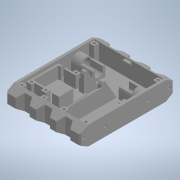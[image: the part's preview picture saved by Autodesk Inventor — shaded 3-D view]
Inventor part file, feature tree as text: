
AUTODESK INVENTOR PART (.ipt)
format: ipt  version: 2020 (Build 240168000, 168)  size: 1,044,992 bytes
history: native  units: in
note: dims shown in document units (in); Inventor stores cm internally (conversion verified against a paired STEP export)
features: projected_geometry x34, extrude x21, sketch x21, mirror x6, plane x1, chamfer x1
ambient origin geometry x8: Origin, YZ Plane, XZ Plane, XY Plane, X Axis, Y Axis, Z Axis, Center Point
bodies: Solid1 (feature_tree)
feature tree (84):
  extrude  "Extrusion1"  Depth=5.9055in
  extrude  "Extrusion2"  TaperAngle=0.0deg  [1 undecoded]
  extrude  "Extrusion3"  Depth=1.063in
  extrude  "Extrusion4"  Depth=0.315in
  extrude  "Extrusion5"  TaperAngle=0.0deg  [1 undecoded]
  extrude  "Extrusion6"  Depth=0.5906in
  mirror  "Mirror1"
  extrude  "Extrusion7"  Depth=0.0787in
  mirror  "Mirror2"
  extrude  "Extrusion8"  Depth=0.6102in
  mirror  "Mirror3"
  plane  "Work Plane1"
  extrude  "Extrusion9"  Depth=0.7874in TaperAngle=0.0deg
  mirror  "Mirror4"
  extrude  "Extrusion10"  Depth=6.063in TaperAngle=0.0deg
  extrude  "Extrusion11"  Depth=0.1575in
  sketch  "Sketch20"  dims[d27=1.5748in d28=0.0in d29=0.0in]
  extrude  "Extrusion17"  TaperAngle=0.0deg  [1 undecoded]
  extrude  "Extrusion19"  Depth=0.2756in
  mirror  "Mirror7"
  extrude  "Extrusion20"  Depth=0.4331in
  extrude  "Extrusion22"  Depth=2.7559in
  extrude  "Extrusion25"  Depth=0.0453in
  extrude  "Extrusion26"  TaperAngle=0.0deg  [1 undecoded]
  extrude  "Extrusion27"  Depth=0.0787in
  extrude  "Extrusion28"  Depth=0.993in
  extrude  "Extrusion29"  Depth=0.2756in
  sketch  "Sketch32"  dims[d46=0.315in d48=0.993in]
  extrude  "Extrusion30"  Depth=0.4724in
  mirror  "Mirror9"
  chamfer  "Chamfer1"  Distance=1.5748in
  sketch  "Sketch39"  dims[d54=0.0in d55=0.4724in d57=1.5748in d58=1.6142in d59=0.1181in d60=0.1969in d89=0.0157in d90=0.0157in d91=0.1476in d92=0.1476in d96=0.315in d97=0.1575in d98=0.1181in d99=0.0in d108=0.0394in d109=0.0in d110=0.063in d111=0.0394in d112=0.0in d121=45.0deg d122=0.993in d123=0.1969in d124=0.3937in d125=0.0in d134=0.3346in d135=0.1772in d138=0.2362in d139=0.3937in d140=0.1969in d141=0.5388in d142=0.1181in d143=1.1024in d144=0.8661in d145=0.0in d146=0.1181in d149=0.315in d151=0.1181in d152=0.0in d153=0.1181in d154=0.0in d155=0.1476in d156=0.2756in d157=0.0in d158=0.5906in d160=0.993in d161=0.1969in d162=45.0deg d163=0.3937in d164=0.0in d168=0.1575in d184=0.1965in d185=0.0in d186=0.0787in d187=0.0787in d188=45.0deg d204=1.5748in d206=1.2761in d207=0.3937in d209=0.3937in d211=0.5118in d213=0.5766in]
  sketch  "Sketch1"  dims[d0=1.1811in d1=5.9055in]
  sketch  "Sketch2"  dims[d2=4.6457in d3=0.0in]
  projected_geometry  "Projected Loop1"
  sketch  "Sketch3"  dims[d4=0.1575in d5=1.063in]
  projected_geometry  "Projected Loop2"
  projected_geometry  "Projected Loop3"
  sketch  "Sketch4"  dims[d6=0.0in d8=0.315in]
  sketch  "Sketch5"  dims[d10=0.993in d11=0.0in]
  projected_geometry  "Projected Loop4"
  sketch  "Sketch6"  dims[d12=0.6496in d13=0.5906in]
  sketch  "Sketch7"  dims[d14=1.5748in d15=0.0787in]
  sketch  "Sketch9"  dims[d16=0.5512in d17=0.0in d18=0.6102in]
  sketch  "Sketch10"  dims[d19=0.4803in d20=0.7874in d21=0.0in]
  sketch  "Sketch12"  dims[d22=0.1654in d23=6.063in d24=0.0in]
  projected_geometry  "Projected Loop6"
  projected_geometry  "Projected Loop7"
  projected_geometry  "Projected Loop8"
  sketch  "Sketch13"  dims[d25=0.5114in d26=0.1575in]
  projected_geometry  "Projected Loop19"
  projected_geometry  "Projected Loop20"
  projected_geometry  "Projected Loop21"
  projected_geometry  "Projected Loop22"
  projected_geometry  "Projected Loop23"
  projected_geometry  "Projected Loop24"
  sketch  "Sketch22"  dims[d30=0.1575in d31=0.2756in]
  sketch  "Sketch23"  dims[d32=0.0in d33=0.4331in]
  sketch  "Sketch26"  dims[d34=0.0906in d38=2.7559in]
  projected_geometry  "Projected Loop25"
  sketch  "Sketch29"  dims[d40=0.0453in d41=0.0909in]
  projected_geometry  "Projected Loop27"
  sketch  "Sketch30"  dims[d42=0.2362in d43=0.0in]
  projected_geometry  "Projected Loop28"
  sketch  "Sketch31"  dims[d44=60.0deg d45=0.0787in]
  projected_geometry  "Projected Loop29"
  sketch  "Sketch33"  dims[d49=0.0in d53=0.2756in]
  projected_geometry  "Projected Loop30"
  projected_geometry  "Projected Loop46"
  projected_geometry  "Projected Loop47"
  projected_geometry  "Projected Loop48"
  projected_geometry  "Projected Loop49"
  projected_geometry  "Projected Loop50"
  projected_geometry  "Projected Loop51"
  projected_geometry  "Projected Loop52"
  projected_geometry  "Projected Loop53"
  projected_geometry  "Projected Loop54"
  projected_geometry  "Projected Loop55"
  projected_geometry  "Projected Loop56"
  projected_geometry  "Projected Loop57"
  projected_geometry  "Projected Loop58"
  projected_geometry  "Projected Loop59"
  projected_geometry  "Project Cut Edges1"
  projected_geometry  "Project Cut Edges2"
note: 4 required parameter values undecoded (feature->parameter linkage not recoverable at this tier; creation-order binding heuristic only, values carry confidence <= 0.55)
